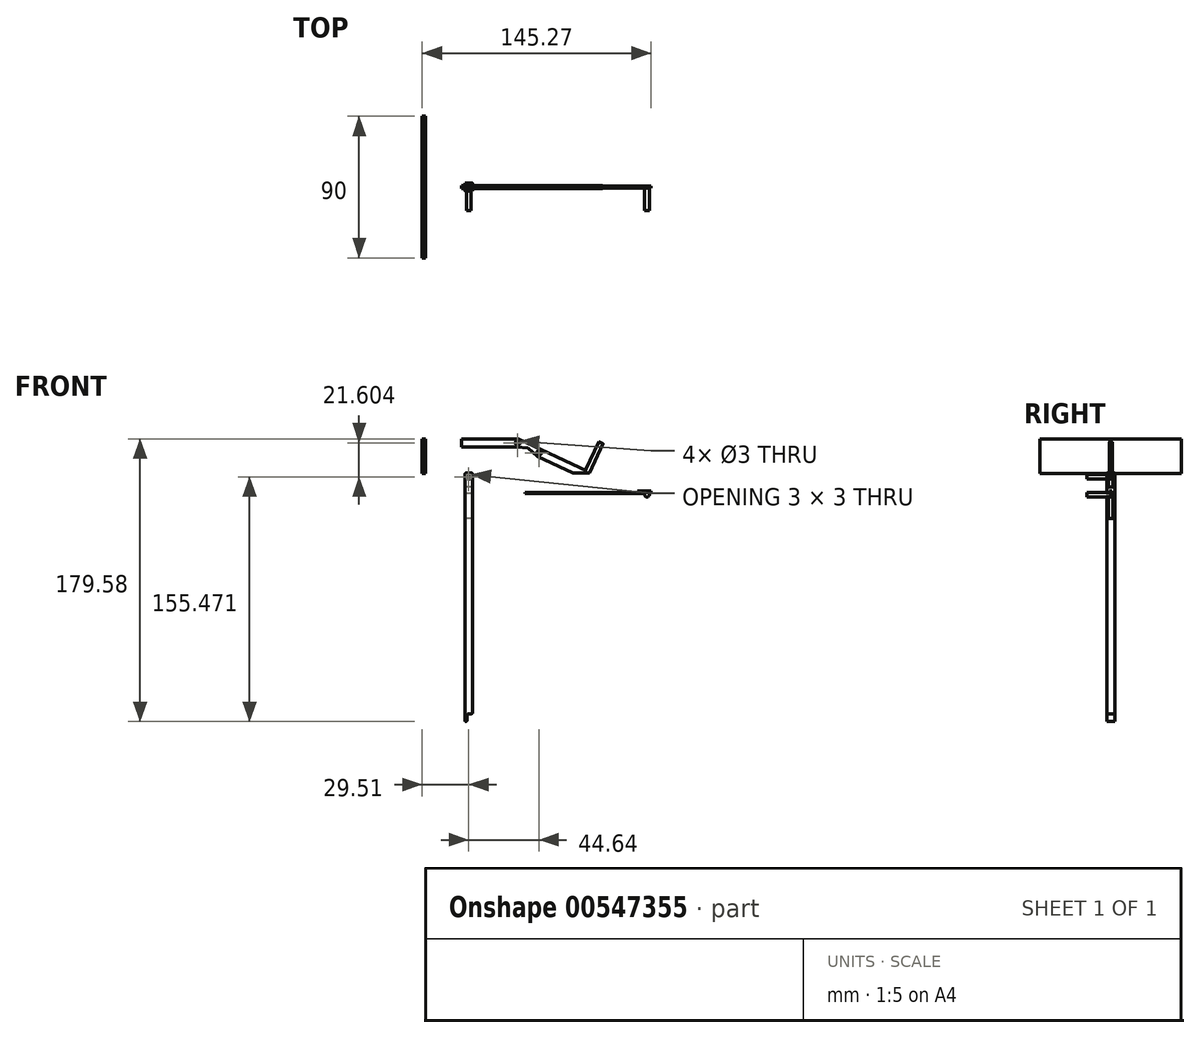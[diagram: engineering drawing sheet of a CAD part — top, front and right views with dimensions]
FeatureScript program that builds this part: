
annotation { "Feature Type Name" : "Feature", "Feature Type Description" : "" }
export const myFeature = defineFeature(function(context is Context, id is Id, definition is map)
    precondition{}
    {
        {
            var Q0;
            Q0=qCreatedBy(makeId("Front.planeOp"),FACE);
            var sketch = newSketch(context, id + "F0", { "sketchPlane" : qUnion([Q0])});
            skLineSegment(sketch, "E0", {"start": v(-142.88, 77.05) * mm, "end": v(-142.88, 55.05) * mm});
            skLineSegment(sketch, "E1", {"start": v(-142.88, 55.05) * mm, "end": v(-140.88, 55.05) * mm});
            skLineSegment(sketch, "E2", {"start": v(-140.88, 55.05) * mm, "end": v(-140.88, 72.05) * mm});
            skLineSegment(sketch, "E3", {"start": v(-140.88, 72.05) * mm, "end": v(-82.88, 72.05) * mm});
            skLineSegment(sketch, "E4", {"start": v(-142.88, 77.05) * mm, "end": v(-81.77, 77.05) * mm});
            skLineSegment(sketch, "E5", {"start": v(-82.88, 72.05) * mm, "end": v(-38.57, 51.38) * mm});
            skLineSegment(sketch, "E6", {"start": v(-38.57, 51.38) * mm, "end": v(-36.45, 55.91) * mm});
            skLineSegment(sketch, "E7", {"start": v(-36.45, 55.91) * mm, "end": v(-81.77, 77.05) * mm});
            skCircle(sketch, "E8", {"center": v(-82.32, 74.55) * mm, "radius": 1.5 * mm});
            skLineSegment(sketch, "E9", {"start": v(-81.77, 77.05) * mm, "end": v(-82.88, 72.05) * mm, "construction": true});
            skCircle(sketch, "E10", {"center": v(-68.73, 68.2) * mm, "radius": 1.5 * mm});
            skLineSegment(sketch, "E11", {"start": v(-82.32, 74.55) * mm, "end": v(-37.51, 53.65) * mm, "construction": true});
            skLineSegment(sketch, "E12.bottom", {"start": v(-115.87, 55.44) * mm, "end": v(-110.87, 55.44) * mm});
            skLineSegment(sketch, "E12.top", {"start": v(-115.87, -102.56) * mm, "end": v(-110.87, -102.56) * mm});
            skLineSegment(sketch, "E12.left", {"start": v(-115.87, 55.44) * mm, "end": v(-115.87, -102.56) * mm});
            skLineSegment(sketch, "E12.right", {"start": v(-110.87, 55.44) * mm, "end": v(-110.87, -102.56) * mm});
            skLineSegment(sketch, "E13", {"start": v(-113.37, 55.44) * mm, "end": v(-113.37, -102.56) * mm, "construction": true});
            skCircle(sketch, "E14", {"center": v(-113.37, 52.94) * mm, "radius": 1.5 * mm});
            skLineSegment(sketch, "E15.bottom", {"start": v(-77.6, 44.13) * mm, "end": v(2.4, 44.13) * mm});
            skLineSegment(sketch, "E15.top", {"start": v(-77.6, 39.13) * mm, "end": v(2.4, 39.13) * mm});
            skLineSegment(sketch, "E15.left", {"start": v(-77.6, 44.13) * mm, "end": v(-77.6, 39.13) * mm});
            skLineSegment(sketch, "E15.right", {"start": v(2.4, 44.13) * mm, "end": v(2.4, 39.13) * mm});
            skLineSegment(sketch, "E16", {"start": v(-77.6, 41.63) * mm, "end": v(2.4, 41.63) * mm, "construction": true});
            skCircle(sketch, "E17", {"center": v(-0.1, 41.63) * mm, "radius": 1.5 * mm});
            skLineSegment(sketch, "E18", {"start": v(-140.88, 72.05) * mm, "end": v(-140.88, 77.05) * mm});
            skLineSegment(sketch, "E19", {"start": v(-115.87, 42.94) * mm, "end": v(-110.87, 42.94) * mm});
            skLineSegment(sketch, "E20", {"start": v(-115.87, 26.94) * mm, "end": v(-110.87, 26.94) * mm});
            skLineSegment(sketch, "E21", {"start": v(-67.67, 70.47) * mm, "end": v(-69.79, 65.94) * mm, "construction": true});
            skLineSegment(sketch, "E22", {"start": v(-36.45, 55.91) * mm, "end": v(-28, 74.04) * mm});
            skLineSegment(sketch, "E23", {"start": v(-28, 74.04) * mm, "end": v(-30.72, 75.3) * mm});
            skLineSegment(sketch, "E24", {"start": v(-30.72, 75.3) * mm, "end": v(-39.17, 57.18) * mm});
            skLineSegment(sketch, "E25", {"start": v(-114.37, -102.56) * mm, "end": v(-114.37, -97.56) * mm});
            skLineSegment(sketch, "E26", {"start": v(-114.37, -97.56) * mm, "end": v(-112.37, -97.56) * mm});
            skLineSegment(sketch, "E27", {"start": v(-112.37, -97.56) * mm, "end": v(-112.37, -102.56) * mm});
            skLineSegment(sketch, "E28", {"start": v(-112.37, -97.56) * mm, "end": v(-110.87, -97.56) * mm});
            skLineSegment(sketch, "E29", {"start": v(-6.23, 44.13) * mm, "end": v(-6.23, 41.63) * mm});
            skLineSegment(sketch, "E30", {"start": v(-6.23, 41.63) * mm, "end": v(-6.23, 39.13) * mm});
            skLineSegment(sketch, "E31", {"start": v(-6.23, 42.88) * mm, "end": v(-77.6, 42.88) * mm});
            skLineSegment(sketch, "E32", {"start": v(-6.23, 40.38) * mm, "end": v(-77.6, 40.38) * mm});
            skLineSegment(sketch, "E33", {"start": v(-82.88, 72.05) * mm, "end": v(-75.55, 71.39) * mm});
            skLineSegment(sketch, "E34", {"start": v(-75.55, 71.39) * mm, "end": v(-69.79, 65.94) * mm});
            skSolve(sketch);
        }
        {
            var Q0;
            {var subQ0=sQuery(id+"F0.wireOp",EDGE,"E31");Q0=makeQuery(id+"F0.imprint","IMPRINT",FACE,{"disambiguationData":[TD([[makeQuery(id+"F0.imprint","IMPRINT",EDGE,{"derivedFrom":subQ0}),1.0]])]});}
            var Q1;
            {var subQ0=sQuery(id+"F0.wireOp",EDGE,"E15.right");Q1=makeQuery(id+"F0.imprint","IMPRINT",FACE,{"disambiguationData":[TD([[makeQuery(id+"F0.imprint","IMPRINT",EDGE,{"derivedFrom":subQ0}),-1.0]])]});}
            extrude(context, id + "F1", {"entities" : qUnion([Q0, Q1]), "endBound" : BoundingType.SYMMETRIC, "depth" : 1.5 * mm, "offsetDistance" : 25 * mm});
        }
        {
            var Q0;
            {var subQ0=sQuery(id+"F0.wireOp",EDGE,"E12.bottom");Q0=makeQuery(id+"F0.imprint","IMPRINT",FACE,{"disambiguationData":[TD([[makeQuery(id+"F0.imprint","IMPRINT",EDGE,{"derivedFrom":subQ0}),-1.0]])]});}
            var Q1;
            {var subQ0=sQuery(id+"F0.wireOp",EDGE,"E20");Q1=makeQuery(id+"F0.imprint","IMPRINT",FACE,{"disambiguationData":[TD([[makeQuery(id+"F0.imprint","IMPRINT",EDGE,{"derivedFrom":subQ0}),-1.0]])]});}
            var Q2;
            {var subQ0=sQuery(id+"F0.wireOp",EDGE,"E19");Q2=makeQuery(id+"F0.imprint","IMPRINT",FACE,{"disambiguationData":[TD([[makeQuery(id+"F0.imprint","IMPRINT",EDGE,{"derivedFrom":subQ0}),-1.0]])]});}
            extrude(context, id + "F2", {"entities" : qUnion([Q0, Q1, Q2]), "endBound" : BoundingType.SYMMETRIC, "depth" : 5 * mm, "offsetDistance" : 25 * mm});
        }
        {
            var Q0;
            Q0=makeQuery(id+"F0.imprint","IMPRINT",FACE,{"disambiguationData":[TD([[makeQuery(id+"F0.imprint","IMPRINT",EDGE,{"derivedFrom":sQuery(id+"F0.wireOp",EDGE,"E3")}),1.0]])]});
            var Q1;
            {var subQ0=sQuery(id+"F0.wireOp",EDGE,"E22");Q1=makeQuery(id+"F0.imprint","IMPRINT",FACE,{"disambiguationData":[TD([[makeQuery(id+"F0.imprint","IMPRINT",EDGE,{"derivedFrom":subQ0}),1.0]])]});}
            extrude(context, id + "F3", {"entities" : qUnion([Q0, Q1]), "endBound" : BoundingType.SYMMETRIC, "depth" : 2 * mm, "offsetDistance" : 25 * mm});
        }
        {
            var Q0;
            {var subQ1=sQuery(id+"F0.wireOp",EDGE,"E0");Q0=makeQuery(id+"F0.imprint","IMPRINT",FACE,{"disambiguationData":[TD([[makeQuery(id+"F0.imprint","IMPRINT",EDGE,{"derivedFrom":subQ1}),1.0]])]});}
            extrude(context, id + "F4", {"entities" : qUnion([Q0]), "endBound" : BoundingType.SYMMETRIC, "depth" : 90 * mm, "offsetDistance" : 25 * mm});
        }
        {
            var Q0;
            Q0=makeQuery(id+"F2.opExtrude","SWEPT_FACE",FACE,{"disambiguationData":[OSD([sQuery(id+"F0.wireOp",EDGE,"E12.left")])]});
            var sketch = newSketch(context, id + "F5", { "sketchPlane" : qUnion([Q0])});
            skLineSegment(sketch, "E35.0", {"start": v(-2.5, 55.44) * mm, "end": v(-2.5, -102.56) * mm});
            skLineSegment(sketch, "E36.0", {"start": v(2.5, 55.44) * mm, "end": v(2.5, -102.56) * mm});
            skLineSegment(sketch, "E37.0", {"start": v(2.5, 55.44) * mm, "end": v(-2.5, 55.44) * mm});
            skLineSegment(sketch, "E38.0", {"start": v(2.5, -102.56) * mm, "end": v(-2.5, -102.56) * mm});
            skLineSegment(sketch, "E39", {"start": v(-2.5, 46.44) * mm, "end": v(2.5, 46.44) * mm});
            skLineSegment(sketch, "E40", {"start": v(-1.5, 55.44) * mm, "end": v(-1.5, 46.44) * mm});
            skLineSegment(sketch, "E41", {"start": v(1.5, 55.44) * mm, "end": v(1.5, 46.44) * mm});
            skLineSegment(sketch, "E42", {"start": v(-2.5, 42.44) * mm, "end": v(2.5, 42.44) * mm});
            skLineSegment(sketch, "E43", {"start": v(-2.5, 26.44) * mm, "end": v(2.5, 26.44) * mm});
            skLineSegment(sketch, "E44", {"start": v(-1.5, 42.44) * mm, "end": v(-1.5, 26.44) * mm});
            skLineSegment(sketch, "E45", {"start": v(1.5, 42.44) * mm, "end": v(1.5, 26.44) * mm});
            skLineSegment(sketch, "E46", {"start": v(-1, -102.56) * mm, "end": v(-1, -97.56) * mm});
            skLineSegment(sketch, "E47", {"start": v(-1, -97.56) * mm, "end": v(1, -97.56) * mm});
            skLineSegment(sketch, "E48", {"start": v(1, -97.56) * mm, "end": v(1, -102.56) * mm});
            skSolve(sketch);
        }
        {
            var Q0;
            {var subQ0=sQuery(id+"F5.wireOp",EDGE,"E40");Q0=makeQuery(id+"F5.imprint","IMPRINT",FACE,{"disambiguationData":[TD([[makeQuery(id+"F5.imprint","IMPRINT",EDGE,{"derivedFrom":subQ0}),1.0]])]});}
            var Q1;
            {var subQ0=sQuery(id+"F5.wireOp",EDGE,"E44");Q1=makeQuery(id+"F5.imprint","IMPRINT",FACE,{"disambiguationData":[TD([[makeQuery(id+"F5.imprint","IMPRINT",EDGE,{"derivedFrom":subQ0}),1.0]])]});}
            extrude(context, id + "F6", {"entities" : qUnion([Q0, Q1]), "operationType" : NewBodyOperationType.REMOVE, "endBound" : BoundingType.THROUGH_ALL, "oppositeDirection" : true, "depth" : 25 * mm, "offsetDistance" : 25 * mm});
        }
        {
            var Q0;
            {var subQ0=sQuery(id+"F0.wireOp",EDGE,"E12.bottom");var subQ1=sQuery(id+"F0.wireOp",EDGE,"E12.right");Q0=makeQuery(id+"F6.boolean.opBoolean","SPLIT",EDGE,{"disambiguationData":[TD([makeQuery(id+"F6.opExtrude","SWEPT_FACE",FACE,{"disambiguationData":[OSD([sQuery(id+"F5.wireOp",EDGE,"E41")])]})])],"derivedFrom":makeQuery(id+"F2.opExtrude","SWEPT_EDGE",EDGE,{"disambiguationData":[OSD([subQ0,subQ1])]})});}
            var Q1;
            {var subQ0=sQuery(id+"F0.wireOp",EDGE,"E12.bottom");var subQ1=sQuery(id+"F0.wireOp",EDGE,"E12.right");Q1=makeQuery(id+"F6.boolean.opBoolean","SPLIT",EDGE,{"disambiguationData":[TD([makeQuery(id+"F6.opExtrude","SWEPT_FACE",FACE,{"disambiguationData":[OSD([sQuery(id+"F5.wireOp",EDGE,"E40")])]})])],"derivedFrom":makeQuery(id+"F2.opExtrude","SWEPT_EDGE",EDGE,{"disambiguationData":[OSD([subQ0,subQ1])]})});}
            var Q2;
            {var subQ0=sQuery(id+"F0.wireOp",EDGE,"E12.bottom");var subQ1=sQuery(id+"F0.wireOp",EDGE,"E12.left");Q2=makeQuery(id+"F6.boolean.opBoolean","SPLIT",EDGE,{"disambiguationData":[TD([makeQuery(id+"F6.opExtrude","SWEPT_FACE",FACE,{"disambiguationData":[OSD([sQuery(id+"F5.wireOp",EDGE,"E40")])]})])],"derivedFrom":makeQuery(id+"F2.opExtrude","SWEPT_EDGE",EDGE,{"disambiguationData":[OSD([subQ0,subQ1])]})});}
            var Q3;
            {var subQ0=sQuery(id+"F0.wireOp",EDGE,"E12.bottom");var subQ1=sQuery(id+"F0.wireOp",EDGE,"E12.left");Q3=makeQuery(id+"F6.boolean.opBoolean","SPLIT",EDGE,{"disambiguationData":[TD([makeQuery(id+"F6.opExtrude","SWEPT_FACE",FACE,{"disambiguationData":[OSD([sQuery(id+"F5.wireOp",EDGE,"E41")])]})])],"derivedFrom":makeQuery(id+"F2.opExtrude","SWEPT_EDGE",EDGE,{"disambiguationData":[OSD([subQ0,subQ1])]})});}
            var Q4;
            Q4=makeQuery(id+"F2.opExtrude","SWEPT_EDGE",EDGE,{"disambiguationData":[OSD([sQuery(id+"F0.wireOp",EDGE,"E25"),sQuery(id+"F0.wireOp",EDGE,"E26")])]});
            var Q5;
            Q5=makeQuery(id+"F2.opExtrude","SWEPT_EDGE",EDGE,{"disambiguationData":[OSD([sQuery(id+"F0.wireOp",EDGE,"E26"),sQuery(id+"F0.wireOp",EDGE,"E27")])]});
            var Q6;
            Q6=makeQuery(id+"F2.opExtrude","SWEPT_EDGE",EDGE,{"disambiguationData":[OSD([sQuery(id+"F0.wireOp",EDGE,"E12.top"),sQuery(id+"F0.wireOp",EDGE,"E25")])]});
            var Q7;
            Q7=makeQuery(id+"F2.opExtrude","SWEPT_EDGE",EDGE,{"disambiguationData":[OSD([sQuery(id+"F0.wireOp",EDGE,"E12.top"),sQuery(id+"F0.wireOp",EDGE,"E27")])]});
            var Q8;
            Q8=makeQuery(id+"F2.opExtrude","SWEPT_EDGE",EDGE,{"disambiguationData":[OSD([sQuery(id+"F0.wireOp",EDGE,"E12.top"),sQuery(id+"F0.wireOp",EDGE,"E12.right")])]});
            var Q9;
            Q9=makeQuery(id+"F2.opExtrude","SWEPT_EDGE",EDGE,{"disambiguationData":[OSD([sQuery(id+"F0.wireOp",EDGE,"E12.top"),sQuery(id+"F0.wireOp",EDGE,"E12.left")])]});
            var Q10;
            Q10=makeQuery(id+"F6.boolean.opBoolean","INTERSECT",EDGE,{"derivedFrom":[makeQuery(id+"F2.opExtrude","SWEPT_FACE",FACE,{"disambiguationData":[OSD([sQuery(id+"F0.wireOp",EDGE,"E12.right")])]}),makeQuery(id+"F6.opExtrude","SWEPT_FACE",FACE,{"disambiguationData":[OSD([sQuery(id+"F5.wireOp",EDGE,"E42")])]})]});
            var Q11;
            Q11=makeQuery(id+"F6.boolean.opBoolean","INTERSECT",EDGE,{"derivedFrom":[makeQuery(id+"F2.opExtrude","SWEPT_FACE",FACE,{"disambiguationData":[OSD([sQuery(id+"F0.wireOp",EDGE,"E12.right")])]}),makeQuery(id+"F6.opExtrude","SWEPT_FACE",FACE,{"disambiguationData":[OSD([sQuery(id+"F5.wireOp",EDGE,"E43")])]})]});
            var Q12;
            Q12=makeQuery(id+"F6.boolean.opBoolean","COPY",EDGE,{"derivedFrom":makeQuery(id+"F6.opExtrude","CAP_EDGE",EDGE,{"disambiguationData":[OSD([sQuery(id+"F5.wireOp",EDGE,"E42")])],"isStart":true})});
            var Q13;
            Q13=makeQuery(id+"F6.boolean.opBoolean","COPY",EDGE,{"derivedFrom":makeQuery(id+"F6.opExtrude","CAP_EDGE",EDGE,{"disambiguationData":[OSD([sQuery(id+"F5.wireOp",EDGE,"E43")])],"isStart":true})});
            var Q14;
            Q14=makeQuery(id+"F6.boolean.opBoolean","COPY",EDGE,{"derivedFrom":makeQuery(id+"F6.opExtrude","CAP_EDGE",EDGE,{"disambiguationData":[OSD([sQuery(id+"F5.wireOp",EDGE,"E39")])],"isStart":true})});
            var Q15;
            Q15=makeQuery(id+"F6.boolean.opBoolean","INTERSECT",EDGE,{"derivedFrom":[makeQuery(id+"F2.opExtrude","SWEPT_FACE",FACE,{"disambiguationData":[OSD([sQuery(id+"F0.wireOp",EDGE,"E12.right")])]}),makeQuery(id+"F6.opExtrude","SWEPT_FACE",FACE,{"disambiguationData":[OSD([sQuery(id+"F5.wireOp",EDGE,"E39")])]})]});
            fillet(context, id + "F7", {"entities" : qUnion([Q0, Q1, Q2, Q3, Q4, Q5, Q6, Q7, Q8, Q9, Q10, Q11, Q12, Q13, Q14, Q15]), "radius" : 1 * mm, "tangentPropagation" : true, "allowEdgeOverflow" : false});
        }
        {
            var Q0;
            Q0=makeQuery(id+"F3.opExtrude","CAP_EDGE",EDGE,{"disambiguationData":[OSD([sQuery(id+"F0.wireOp",EDGE,"E6"),sQuery(id+"F0.wireOp",EDGE,"E22")])],"isStart":false});
            var Q1;
            Q1=makeQuery(id+"F3.opExtrude","CAP_EDGE",EDGE,{"disambiguationData":[OSD([sQuery(id+"F0.wireOp",EDGE,"E6"),sQuery(id+"F0.wireOp",EDGE,"E22")])],"isStart":true});
            var Q2;
            Q2=makeQuery(id+"F3.opExtrude","CAP_EDGE",EDGE,{"disambiguationData":[OSD([sQuery(id+"F0.wireOp",EDGE,"E24")])],"isStart":true});
            var Q3;
            Q3=makeQuery(id+"F3.opExtrude","CAP_EDGE",EDGE,{"disambiguationData":[OSD([sQuery(id+"F0.wireOp",EDGE,"E24")])],"isStart":false});
            fillet(context, id + "F8", {"entities" : qUnion([Q0, Q1, Q2, Q3]), "radius" : 1 * mm, "tangentPropagation" : true, "allowEdgeOverflow" : false});
        }
        {
            var Q0;
            Q0=makeQuery(id+"F4.opExtrude","SWEPT_FACE",FACE,{"disambiguationData":[OSD([sQuery(id+"F0.wireOp",EDGE,"E0")])]});
            var sketch = newSketch(context, id + "F9", { "sketchPlane" : qUnion([Q0])});
            skLineSegment(sketch, "E49.0.0", {"start": v(-1, 77.05) * mm, "end": v(-1, 72.05) * mm});
            skLineSegment(sketch, "E49.0.1", {"start": v(-1, 72.05) * mm, "end": v(1, 72.05) * mm});
            skLineSegment(sketch, "E49.0.2", {"start": v(1, 72.05) * mm, "end": v(1, 77.05) * mm});
            skLineSegment(sketch, "E49.0.3", {"start": v(1, 77.05) * mm, "end": v(-1, 77.05) * mm});
            skSolve(sketch);
        }
        {
            var Q0;
            Q0=makeQuery(id+"F9.imprint","IMPRINT",FACE,{"disambiguationData":[TD([[makeQuery(id+"F9.imprint","IMPRINT",EDGE,{"derivedFrom":sQuery(id+"F9.wireOp",EDGE,"E49.0.0")}),1.0]])]});
            extrude(context, id + "F10", {"entities" : qUnion([Q0]), "operationType" : NewBodyOperationType.REMOVE, "oppositeDirection" : true, "depth" : 25 * mm, "offsetDistance" : 25 * mm});
        }
        {
            var Q0;
            Q0=makeQuery(id+"F0.imprint","IMPRINT",FACE,{"disambiguationData":[TD([[makeQuery(id+"F0.imprint","IMPRINT",EDGE,{"derivedFrom":sQuery(id+"F0.wireOp",EDGE,"E14")}),1.0]])]});
            var Q1;
            Q1=makeQuery(id+"F0.imprint","IMPRINT",FACE,{"disambiguationData":[TD([[makeQuery(id+"F0.imprint","IMPRINT",EDGE,{"derivedFrom":sQuery(id+"F0.wireOp",EDGE,"E17")}),1.0]])]});
            extrude(context, id + "F11", {"entities" : qUnion([Q0, Q1]), "depth" : 15 * mm, "offsetDistance" : 25 * mm});
        }
    });
